# Revit family: Door_Sliding_Aluminum_WesternWindow_600-MultiSlide
name_source: partatom
category: Doors
revit_build: Autodesk Revit 2014 (Build: 20130308_1515(x64)
units: mm (PartAtom-declared; Revit-internal decimal feet)

## types (12) — shared parameters
AAMA Designation = as Specified
Air Infiltration = as Specified
Analytic Construction = <None>
Description = Western Window Aluminum Stacking Sliding Door - 600 Multi-Slide as Specified
Fire Rating = As Specified
Function = Interior
Handle CL Elevation = 3' - 2"
Heat Transfer Coefficient (U) = 1 BTU/(h·ft²·°F)
Manufacturer = Western Window Systems
Manufacturer Fax = 602-243-3119
Manufacturer Website = https://www.westernwindowsystems.com
Maximum Size = as Specified
Miami Dade Conformance = as Specified
Model = 600 Multi-Slide Door
Operation = as Specified
Panel Thickness = 0' - 1 7/16"
Product Data = http://www.arcat.com
Product Properties = https://www.westernwindowsystems.com
R = 0.0000 (h·ft²·°F)/BTU
RO Offset = 0' - 0 1/2"
Sales Information = https://www.westernwindowsystems.com
Standards Conformance = as Specified
Structural Test Pressure = as Specified
Thermal Resistance (R) = 0.0000 (h·ft²·°F)/BTU
Thickness = 0' - 0"
U = 1 BTU/(h·ft²·°F)
URL = https://www.westernwindowsystems.com
Wall Closure = By host
Water Penetration = as Specified
zero-valued in all types: Expected Lifespan (Years), Maintenance Schedule (Months), SHGC, Solar Heat Gain Coefficient, VLT, Visual Light Transmittance, Warranty Duration (Years)

## per-type parameters (varying)
| type | Frame Depth | Frame Type | Number of Operable Panels |
| 4 Active Panel Thermally Broken Water Barrier Sill | 0' - 9 25/32" | 600SMultiSlide : Water Barrier Sill | 4 |
| 4 Active Panel Thermally Broken Flush Sill | 0' - 9 25/32" | 600SMultiSlide : Flush Sill | 4 |
| 4 Active Panel Classic Water Barrier Sill | 0' - 9 25/32" | 600SMultiSlide : Water Barrier Sill | 4 |
| 4 Active Panel Classic Flush Sill | 0' - 9 25/32" | 600SMultiSlide : Flush Sill | 4 |
| 3 Active Panel Thermally Broken Water Barrier Sill | 0' - 7 27/32" | 600SMultiSlide : Water Barrier Sill | 3 |
| 3 Active Panel Thermally Broken Flush Sill | 0' - 7 27/32" | 600SMultiSlide : Flush Sill | 3 |
| 3 Active Panel Classic Water Barrier Sill | 0' - 7 27/32" | 600SMultiSlide : Water Barrier Sill | 3 |
| 3 Active Panel Classic Flush Sill | 0' - 7 27/32" | 600SMultiSlide : Flush Sill | 3 |
| 2 Active Panel Classic Flush Sill | 0' - 5 7/8" | 600SMultiSlide : Flush Sill | 2 |
| 2 Active Panel Classic Water Barrier Sill | 0' - 5 7/8" | 600SMultiSlide : Water Barrier Sill | 2 |
| 2 Active Panel Thermally Broken Flush Sill | 0' - 5 7/8" | 600SMultiSlide : Flush Sill | 2 |
| 2 Active Panel Thermally Broken Water Barrier Sill | 0' - 5 7/8" | 600SMultiSlide : Water Barrier Sill | 2 |

## geometry (parser evidence)
native form markers: Sweep x15
no freeform markers — native parametric forms only
